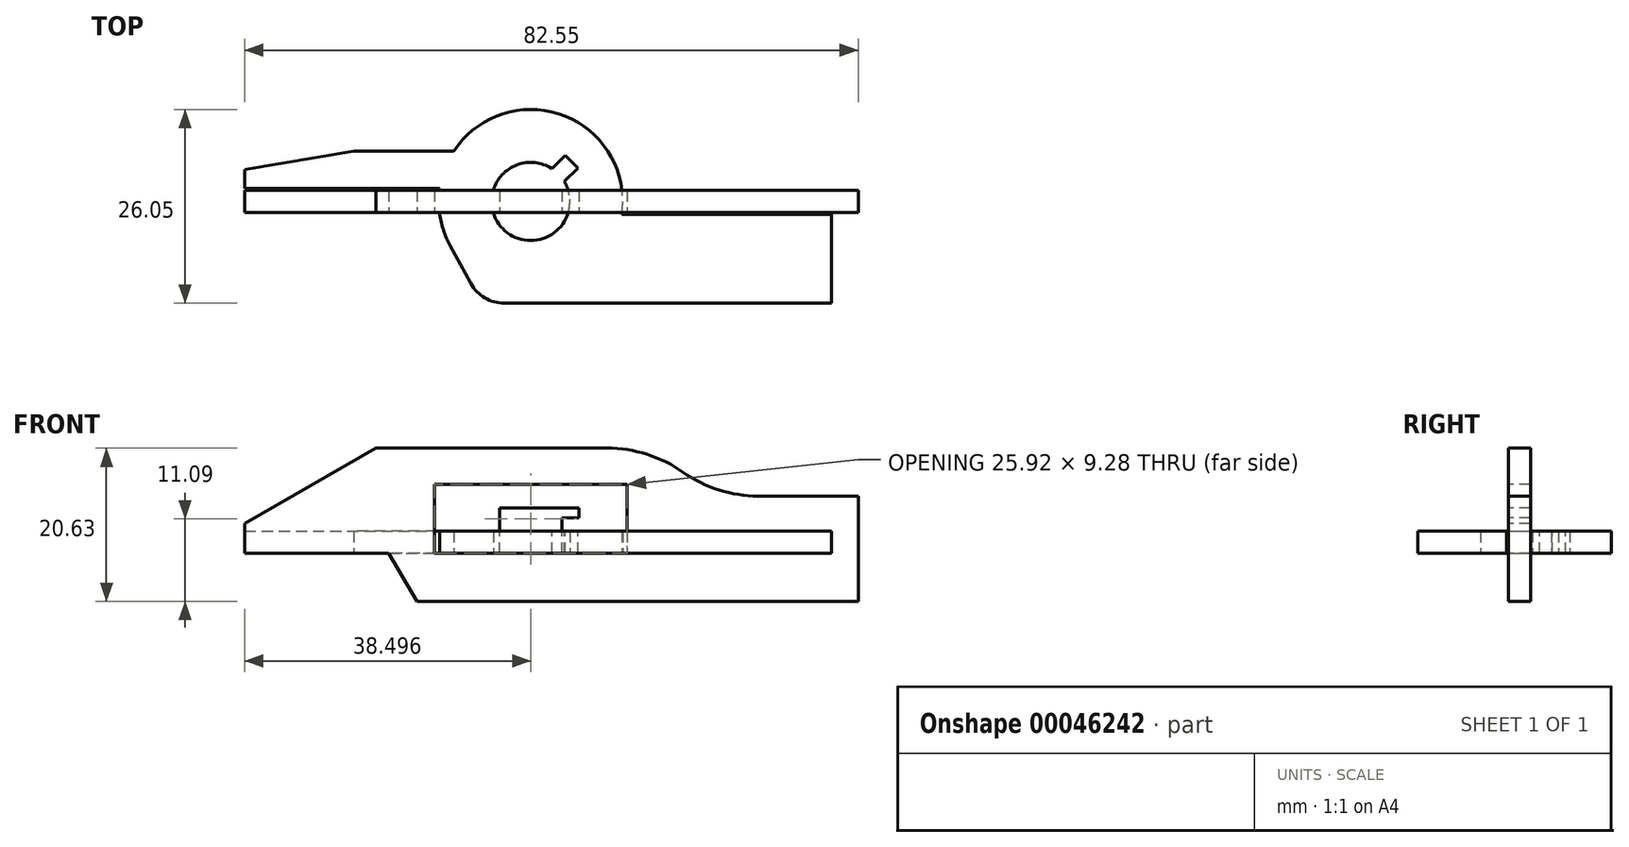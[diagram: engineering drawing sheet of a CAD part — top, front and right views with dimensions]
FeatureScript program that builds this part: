
annotation { "Feature Type Name" : "Feature", "Feature Type Description" : "" }
export const myFeature = defineFeature(function(context is Context, id is Id, definition is map)
    precondition{}
    {
        {
            var Q0;
            Q0=qCreatedBy(makeId("Front.planeOp"),FACE);
            var sketch = newSketch(context, id + "F0", { "sketchPlane" : qUnion([Q0])});
            skLineSegment(sketch, "E0.rect.bottom", {"start": v(41.28, 28.58) * mm, "end": v(-41.28, 28.58) * mm});
            skLineSegment(sketch, "E0.rect.top", {"start": v(41.28, -28.58) * mm, "end": v(-41.28, -28.58) * mm});
            skLineSegment(sketch, "E0.rect.left", {"start": v(41.28, 28.58) * mm, "end": v(41.28, -28.58) * mm});
            skLineSegment(sketch, "E0.rect.right", {"start": v(-41.28, 28.58) * mm, "end": v(-41.28, -28.58) * mm});
            skPoint(sketch, "E0.rect.middle", {"position": v(0, 0) * mm});
            skSolve(sketch);
        }
        {
            var Q0;
            Q0=makeQuery(id+"F0.imprint","IMPRINT",FACE,{"disambiguationData":[TD([[makeQuery(id+"F0.imprint","IMPRINT",EDGE,{"derivedFrom":sQuery(id+"F0.wireOp",EDGE,"E0.rect.bottom")}),1.0]])]});
            extrude(context, id + "F1", {"entities" : qUnion([Q0]), "endBound" : BoundingType.SYMMETRIC, "depth" : 3 * mm});
        }
        {
            var Q0;
            Q0=makeQuery(id+"F1.opExtrude","CAP_FACE",FACE,{"disambiguationData":[OSD([sQuery(id+"F0.wireOp",EDGE,"E0.rect.bottom"),sQuery(id+"F0.wireOp",EDGE,"E0.rect.top"),sQuery(id+"F0.wireOp",EDGE,"E0.rect.left"),sQuery(id+"F0.wireOp",EDGE,"E0.rect.right")])],"isStart":false});
            var sketch = newSketch(context, id + "F2", { "sketchPlane" : qUnion([Q0])});
            skLineSegment(sketch, "E1.0", {"start": v(-41.28, 28.58) * mm, "end": v(-41.28, -28.58) * mm});
            skLineSegment(sketch, "E2.0", {"start": v(41.28, 28.58) * mm, "end": v(-41.28, 28.58) * mm});
            skLineSegment(sketch, "E3.0", {"start": v(41.28, 28.58) * mm, "end": v(41.28, -28.58) * mm});
            skLineSegment(sketch, "E4.0", {"start": v(41.28, -28.58) * mm, "end": v(-41.28, -28.58) * mm});
            skLineSegment(sketch, "E5", {"start": v(-41.28, 0) * mm, "end": v(7.45, 0) * mm});
            skArc(sketch, "E6", {"start": v(7.45, 0) * mm, "mid": v(12.86, -0.84) * mm, "end": v(17.76, -3.27) * mm});
            skLineSegment(sketch, "E7", {"start": v(27.8, -6.45) * mm, "end": v(41.28, -6.45) * mm});
            skLineSegment(sketch, "E8", {"start": v(-41.28, -14.18) * mm, "end": v(-21.87, -14.18) * mm});
            skLineSegment(sketch, "E9", {"start": v(-21.87, -14.18) * mm, "end": v(-18.05, -20.63) * mm});
            skLineSegment(sketch, "E10", {"start": v(-18.05, -20.63) * mm, "end": v(41.28, -20.63) * mm});
            skArc(sketch, "E11", {"start": v(17.76, -3.27) * mm, "mid": v(22.53, -5.64) * mm, "end": v(27.8, -6.45) * mm});
            skLineSegment(sketch, "E12.bottom", {"start": v(-15.75, -4.9) * mm, "end": v(10.18, -4.9) * mm});
            skLineSegment(sketch, "E12.top", {"start": v(-15.75, -14.18) * mm, "end": v(10.18, -14.18) * mm});
            skLineSegment(sketch, "E12.left", {"start": v(-15.75, -4.9) * mm, "end": v(-15.75, -14.18) * mm});
            skLineSegment(sketch, "E12.right", {"start": v(10.18, -4.9) * mm, "end": v(10.18, -14.18) * mm});
            skLineSegment(sketch, "E13.top", {"start": v(10.18, -4.9) * mm, "end": v(-15.75, -4.9) * mm});
            skLineSegment(sketch, "E13.right", {"start": v(-15.75, -10.68) * mm, "end": v(-15.75, -4.9) * mm});
            skLineSegment(sketch, "E14.bottom", {"start": v(-6.95, -14.18) * mm, "end": v(1.38, -14.18) * mm});
            skLineSegment(sketch, "E14.top", {"start": v(-6.95, -9.37) * mm, "end": v(1.38, -9.37) * mm});
            skLineSegment(sketch, "E14.left", {"start": v(-6.95, -14.18) * mm, "end": v(-6.95, -9.37) * mm});
            skLineSegment(sketch, "E14.right", {"start": v(1.38, -14.18) * mm, "end": v(1.38, -9.37) * mm});
            skLineSegment(sketch, "E15", {"start": v(-23.63, 0) * mm, "end": v(-41.28, -10.14) * mm});
            skLineSegment(sketch, "E16", {"start": v(-2.78, -4.9) * mm, "end": v(-2.78, -14.18) * mm});
            skPoint(sketch, "E17", {"position": v(-2.78, -14.18) * mm});
            skLineSegment(sketch, "E18.bottom", {"start": v(-6.95, -8.04) * mm, "end": v(3.67, -8.04) * mm});
            skLineSegment(sketch, "E18.top", {"start": v(-6.95, -9.37) * mm, "end": v(3.67, -9.37) * mm});
            skLineSegment(sketch, "E18.left", {"start": v(-6.95, -8.04) * mm, "end": v(-6.95, -9.37) * mm});
            skLineSegment(sketch, "E18.right", {"start": v(3.67, -8.04) * mm, "end": v(3.67, -9.37) * mm});
            skSolve(sketch);
        }
        {
            var Q0;
            {var subQ2=sQuery(id+"F2.wireOp",EDGE,"E2.0");Q0=makeQuery(id+"F2.imprint","IMPRINT",FACE,{"disambiguationData":[TD([[makeQuery(id+"F2.imprint","IMPRINT",EDGE,{"derivedFrom":subQ2}),1.0]])]});}
            var Q1;
            {var subQ2=sQuery(id+"F2.wireOp",EDGE,"E4.0");Q1=makeQuery(id+"F2.imprint","IMPRINT",FACE,{"disambiguationData":[TD([[makeQuery(id+"F2.imprint","IMPRINT",EDGE,{"derivedFrom":subQ2}),-1.0]])]});}
            var Q2;
            {var subQ4=sQuery(id+"F2.wireOp",EDGE,"E12.left");Q2=makeQuery(id+"F2.imprint","IMPRINT",FACE,{"disambiguationData":[TD([[makeQuery(id+"F2.imprint","IMPRINT",EDGE,{"derivedFrom":subQ4}),1.0]])]});}
            var Q3;
            {var subQ0=sQuery(id+"F2.wireOp",EDGE,"E15");Q3=makeQuery(id+"F2.imprint","IMPRINT",FACE,{"disambiguationData":[TD([[makeQuery(id+"F2.imprint","IMPRINT",EDGE,{"derivedFrom":subQ0}),-1.0]])]});}
            var Q4;
            {var subQ7=sQuery(id+"F2.wireOp",EDGE,"E12.right");Q4=makeQuery(id+"F2.imprint","IMPRINT",FACE,{"disambiguationData":[TD([[makeQuery(id+"F2.imprint","IMPRINT",EDGE,{"derivedFrom":subQ7}),-1.0]])]});}
            extrude(context, id + "F3", {"entities" : qUnion([Q0, Q1, Q2, Q3, Q4]), "operationType" : NewBodyOperationType.REMOVE, "oppositeDirection" : true, "depth" : 25.4 * mm});
        }
        {
            var Q0;
            {var subQ0=sQuery(id+"F2.wireOp",EDGE,"E12.top");Q0=makeQuery(id+"F3.boolean.opBoolean","COPY",FACE,{"derivedFrom":makeQuery(id+"F3.opExtrude","SWEPT_FACE",FACE,{"disambiguationData":[OSD([subQ0]),TDD([makeQuery(id+"F2.imprint","IMPRINT",EDGE,{"disambiguationData":[TD([[makeQuery(id+"F2.imprint","INTERSECT",VERTEX,{"derivedFrom":[subQ0,sQuery(id+"F2.wireOp",EDGE,"E12.left")]}),-1.0]])],"derivedFrom":subQ0})])]})});}
            var sketch = newSketch(context, id + "F4", { "sketchPlane" : qUnion([Q0])});
            skLineSegment(sketch, "E19.0.0", {"start": v(-15.75, 1.5) * mm, "end": v(-15.75, -1.5) * mm});
            skLineSegment(sketch, "E19.0.2", {"start": v(-15.75, -1.5) * mm, "end": v(-15.75, 1.5) * mm});
            skLineSegment(sketch, "E20.0", {"start": v(-6.95, 1.5) * mm, "end": v(-6.95, -1.5) * mm});
            skLineSegment(sketch, "E21.0", {"start": v(10.18, 1.5) * mm, "end": v(10.18, -1.5) * mm});
            skLineSegment(sketch, "E22.0", {"start": v(1.38, 1.5) * mm, "end": v(1.38, -1.5) * mm});
            skLineSegment(sketch, "E23.0", {"start": v(-41.27, 1.5) * mm, "end": v(-41.27, -1.5) * mm});
            skLineSegment(sketch, "E24", {"start": v(-41.27, 1.75) * mm, "end": v(-15.03, 1.75) * mm});
            skLineSegment(sketch, "E25", {"start": v(-41.27, 1.75) * mm, "end": v(-41.27, 4.32) * mm});
            skLineSegment(sketch, "E26", {"start": v(-41.27, 4.32) * mm, "end": v(-26.6, 6.77) * mm});
            skLineSegment(sketch, "E27.0", {"start": v(7.45, -1.5) * mm, "end": v(7.45, 1.5) * mm});
            skLineSegment(sketch, "E28", {"start": v(7.17, 6.77) * mm, "end": v(-26.6, 6.77) * mm});
            skLineSegment(sketch, "E29", {"start": v(-13.63, -5.95) * mm, "end": v(-9.39, -13.68) * mm});
            skLineSegment(sketch, "E30", {"start": v(-9.39, -13.68) * mm, "end": v(37.7, -13.68) * mm});
            skLineSegment(sketch, "E31", {"start": v(37.7, -13.68) * mm, "end": v(37.7, -1.75) * mm});
            skLineSegment(sketch, "E32", {"start": v(37.7, -1.75) * mm, "end": v(9.46, -1.75) * mm});
            skLineSegment(sketch, "E33", {"start": v(-6.95, 0) * mm, "end": v(1.38, 0) * mm});
            skPoint(sketch, "E34", {"position": v(-2.78, 0) * mm});
            skPoint(sketch, "E35", {"position": v(-2.79, 0) * mm});
            skPoint(sketch, "E36", {"position": v(-1.02, 0) * mm});
            skPoint(sketch, "E37", {"position": v(-4.95, 0) * mm});
            skCircle(sketch, "E38", {"center": v(-2.78, 0) * mm, "radius": 5.26 * mm});
            skCircle(sketch, "E39", {"center": v(-2.78, 0) * mm, "radius": 12.37 * mm});
            skSolve(sketch);
        }
        {
            var Q0;
            {var subQ4=sQuery(id+"F4.wireOp",EDGE,"E24");Q0=makeQuery(id+"F4.imprint","IMPRINT",FACE,{"disambiguationData":[TD([[makeQuery(id+"F4.imprint","IMPRINT",EDGE,{"derivedFrom":subQ4}),1.0]])]});}
            var Q1;
            {var subQ2=sQuery(id+"F4.wireOp",EDGE,"E29");Q1=makeQuery(id+"F4.imprint","IMPRINT",FACE,{"disambiguationData":[TD([[makeQuery(id+"F4.imprint","IMPRINT",EDGE,{"derivedFrom":subQ2}),1.0]])]});}
            var Q2;
            {var subQ5=sQuery(id+"F4.wireOp",EDGE,"E39");var subQ12=makeQuery(id+"F4.imprint","INTERSECT",VERTEX,{"derivedFrom":[sQuery(id+"F4.wireOp",EDGE,"E24"),subQ5]});Q2=makeQuery(id+"F4.imprint","IMPRINT",FACE,{"disambiguationData":[TD([[makeQuery(id+"F4.imprint","IMPRINT",EDGE,{"disambiguationData":[TD([[subQ12,1.0]])],"derivedFrom":subQ5}),1.0]])]});}
            var Q3;
            {var subQ0=sQuery(id+"F2.wireOp",EDGE,"E12.top");var subQ1=makeQuery(id+"F2.imprint","IMPRINT",EDGE,{"disambiguationData":[TD([[makeQuery(id+"F2.imprint","INTERSECT",VERTEX,{"derivedFrom":[subQ0,sQuery(id+"F2.wireOp",EDGE,"E12.left")]}),-1.0]])],"derivedFrom":subQ0});var subQ2=makeQuery(id+"F3.boolean.opBoolean","COPY",EDGE,{"derivedFrom":makeQuery(id+"F3.opExtrude","CAP_EDGE",EDGE,{"disambiguationData":[OSD([subQ0]),TDD([subQ1])],"isStart":true})});var subQ5=sQuery(id+"F4.wireOp",EDGE,"E39");var subQ6=makeQuery(id+"F4.imprint","INTERSECT",VERTEX,{"derivedFrom":[subQ2,subQ5]});Q3=makeQuery(id+"F4.imprint","IMPRINT",FACE,{"disambiguationData":[TD([[makeQuery(id+"F4.imprint","IMPRINT",EDGE,{"disambiguationData":[TD([[subQ6,-1.0]])],"derivedFrom":subQ2}),1.0]])]});}
            extrude(context, id + "F5", {"entities" : qUnion([Q0, Q1, Q2, Q3]), "depth" : 3 * mm});
        }
        {
            var Q0;
            Q0=makeQuery(id+"F5.opExtrude","SWEPT_EDGE",EDGE,{"disambiguationData":[OSD([sQuery(id+"F4.wireOp",EDGE,"E29"),sQuery(id+"F4.wireOp",EDGE,"E30")])]});
            fillet(context, id + "F6", {"entities" : qUnion([Q0]), "radius" : 5.08 * mm, "tangentPropagation" : true, "allowEdgeOverflow" : false});
        }
        {
            var Q0;
            Q0=makeQuery(id+"F5.opExtrude","CAP_FACE",FACE,{"disambiguationData":[OSD([sQuery(id+"F4.wireOp",EDGE,"E24"),sQuery(id+"F4.wireOp",EDGE,"E25"),sQuery(id+"F4.wireOp",EDGE,"E26"),sQuery(id+"F4.wireOp",EDGE,"E28"),sQuery(id+"F4.wireOp",EDGE,"E29"),sQuery(id+"F4.wireOp",EDGE,"E30"),sQuery(id+"F4.wireOp",EDGE,"E31"),sQuery(id+"F4.wireOp",EDGE,"E32"),sQuery(id+"F4.wireOp",EDGE,"E38"),sQuery(id+"F4.wireOp",EDGE,"E39")])],"isStart":false});
            var sketch = newSketch(context, id + "F7", { "sketchPlane" : qUnion([Q0])});
            skCircle(sketch, "E40.0", {"center": v(-2.78, 0) * mm, "radius": 5.26 * mm});
            skLineSegment(sketch, "E41", {"start": v(1.73, 2.69) * mm, "end": v(3.56, 4.45) * mm});
            skLineSegment(sketch, "E42", {"start": v(3.56, 4.45) * mm, "end": v(1.88, 6.19) * mm});
            skLineSegment(sketch, "E43", {"start": v(1.88, 6.19) * mm, "end": v(0.06, 4.42) * mm});
            skLineSegment(sketch, "E44", {"start": v(-2.78, 0) * mm, "end": v(2.72, 5.32) * mm});
            skLineSegment(sketch, "E45.0", {"start": v(-6.38, -13.68) * mm, "end": v(37.7, -13.68) * mm});
            skSolve(sketch);
        }
        {
            var Q0;
            {var subQ0=sQuery(id+"F7.wireOp",EDGE,"E41");Q0=makeQuery(id+"F7.imprint","IMPRINT",FACE,{"disambiguationData":[TD([[makeQuery(id+"F7.imprint","IMPRINT",EDGE,{"derivedFrom":subQ0}),1.0]])]});}
            var Q1;
            {var subQ5=sQuery(id+"F7.wireOp",EDGE,"E43");Q1=makeQuery(id+"F7.imprint","IMPRINT",FACE,{"disambiguationData":[TD([[makeQuery(id+"F7.imprint","IMPRINT",EDGE,{"derivedFrom":subQ5}),1.0]])]});}
            extrude(context, id + "F8", {"entities" : qUnion([Q0, Q1]), "operationType" : NewBodyOperationType.REMOVE, "oppositeDirection" : true, "depth" : 25.4 * mm});
        }
    });
